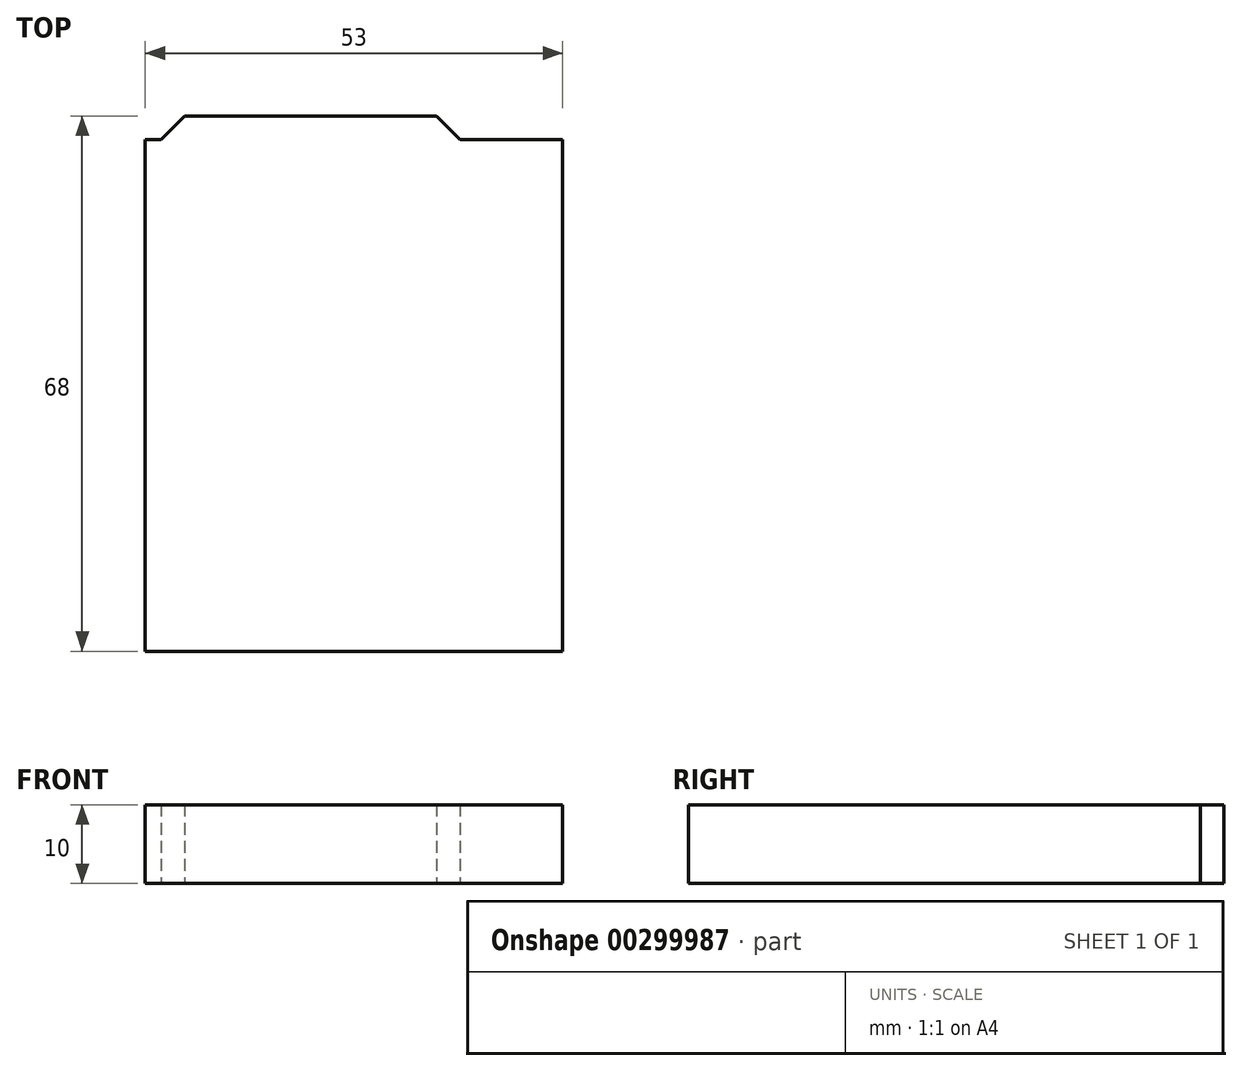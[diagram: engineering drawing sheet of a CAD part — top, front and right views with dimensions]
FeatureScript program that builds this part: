
annotation { "Feature Type Name" : "Feature", "Feature Type Description" : "" }
export const myFeature = defineFeature(function(context is Context, id is Id, definition is map)
    precondition{}
    {
        {
            var Q0;
            Q0=qCreatedBy(makeId("Top.planeOp"),FACE);
            var sketch = newSketch(context, id + "F0", { "sketchPlane" : qUnion([Q0])});
            skLineSegment(sketch, "E0.bottom", {"start": v(0, 0) * mm, "end": v(53, 0) * mm});
            skLineSegment(sketch, "E0.top", {"start": v(0, 65) * mm, "end": v(53, 65) * mm});
            skLineSegment(sketch, "E0.left", {"start": v(0, 0) * mm, "end": v(0, 65) * mm});
            skLineSegment(sketch, "E0.right", {"start": v(53, 0) * mm, "end": v(53, 65) * mm});
            skLineSegment(sketch, "E1", {"start": v(2, 65) * mm, "end": v(5, 68) * mm});
            skLineSegment(sketch, "E2", {"start": v(5, 68) * mm, "end": v(37, 68) * mm});
            skLineSegment(sketch, "E3", {"start": v(37, 68) * mm, "end": v(40, 65) * mm});
            skSolve(sketch);
        }
        {
            var Q0;
            Q0 = qSketchRegion(id + "F0", true);
            extrude(context, id + "F1", {"entities" : qUnion([Q0]), "depth" : 10 * mm});
        }
    });
